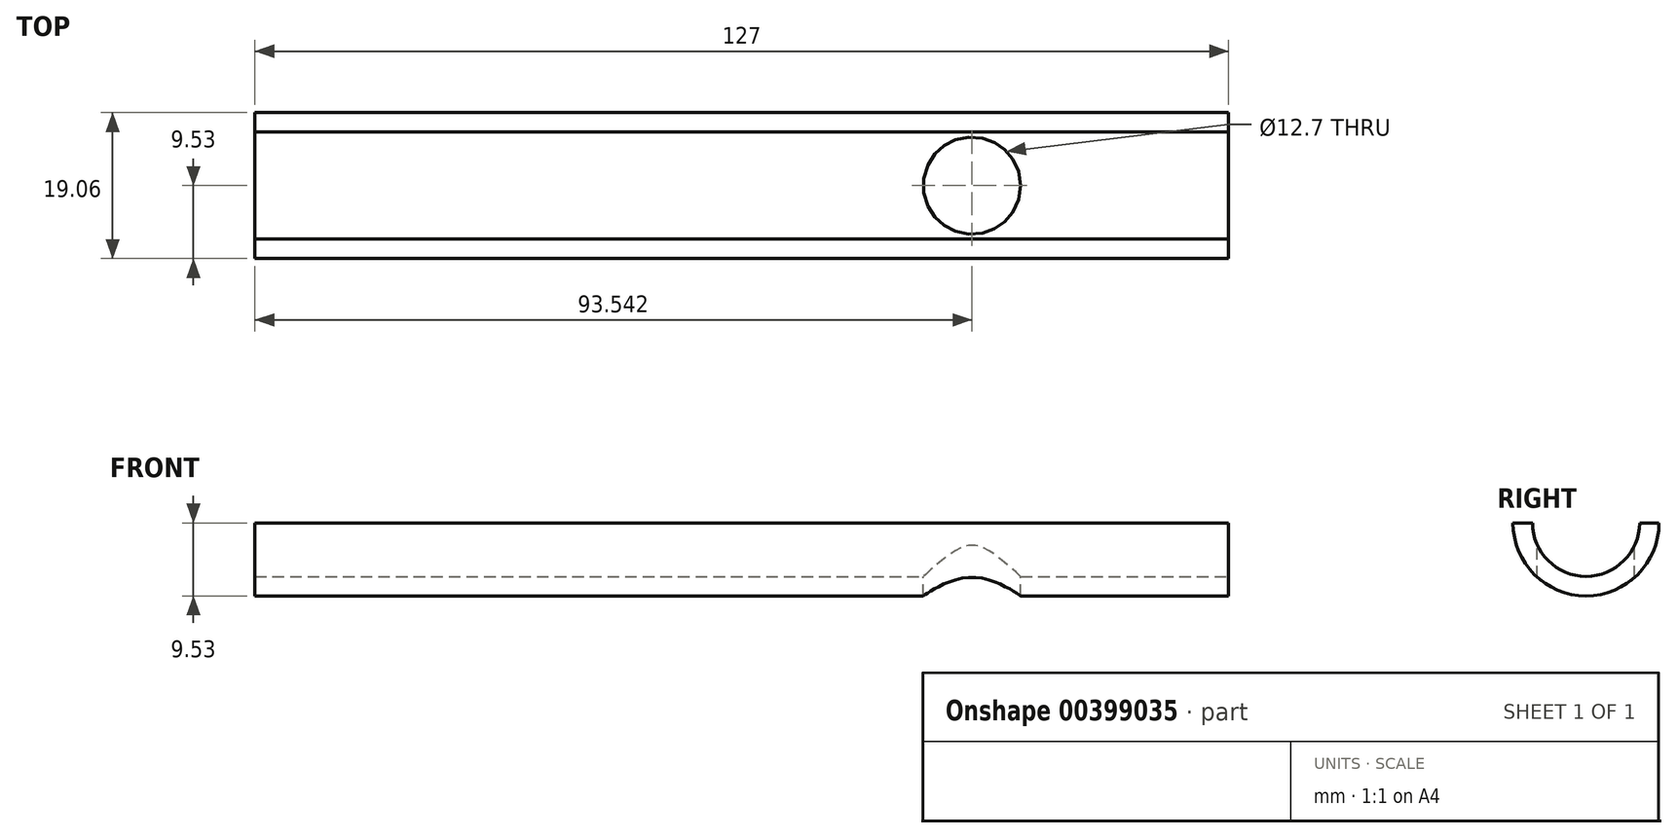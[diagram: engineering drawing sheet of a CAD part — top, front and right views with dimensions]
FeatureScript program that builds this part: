
annotation { "Feature Type Name" : "Feature", "Feature Type Description" : "" }
export const myFeature = defineFeature(function(context is Context, id is Id, definition is map)
    precondition{}
    {
        {
            var Q0;
            Q0=qCreatedBy(makeId("Right.planeOp"),FACE);
            var sketch = newSketch(context, id + "F0", { "sketchPlane" : qUnion([Q0])});
            skArc(sketch, "E0", {"start": v(-9.53, 0) * mm, "mid": v(0, -9.53) * mm, "end": v(9.53, 0) * mm});
            skLineSegment(sketch, "E1", {"start": v(-9.53, 0) * mm, "end": v(9.53, 0) * mm});
            skSolve(sketch);
        }
        {
            var Q0;
            Q0 = qSketchRegion(id + "F0", true);
            extrude(context, id + "F1", {"entities" : qUnion([Q0]), "oppositeDirection" : true, "depth" : 127 * mm, "symmetric" : true});
        }
        {
            var Q0;
            Q0=makeQuery(id+"F1.opExtrude","CAP_FACE",FACE,{"disambiguationData":[OSD([sQuery(id+"F0.wireOp",EDGE,"E0"),sQuery(id+"F0.wireOp",EDGE,"E1")])],"isStart":false});
            var Q1;
            Q1=makeQuery(id+"F1.opExtrude","SWEPT_FACE",FACE,{"disambiguationData":[OSD([sQuery(id+"F0.wireOp",EDGE,"E1")])]});
            var Q2;
            Q2=makeQuery(id+"F1.opExtrude","CAP_FACE",FACE,{"disambiguationData":[OSD([sQuery(id+"F0.wireOp",EDGE,"E0"),sQuery(id+"F0.wireOp",EDGE,"E1")])],"isStart":true});
            shell(context, id + "F2", {"entities" : qUnion([Q0, Q1, Q2]), "thickness" : 2.54 * mm});
        }
        {
            var Q0;
            Q0=qCreatedBy(makeId("Top.planeOp"),FACE);
            var sketch = newSketch(context, id + "F3", { "sketchPlane" : qUnion([Q0])});
            skCircle(sketch, "E2", {"center": v(30.04, 0) * mm, "radius": 6.35 * mm});
            skSolve(sketch);
        }
        {
            var Q0;
            Q0=makeQuery(id+"F3.imprint","IMPRINT",FACE,{"disambiguationData":[TD([[makeQuery(id+"F3.imprint","IMPRINT",EDGE,{"derivedFrom":sQuery(id+"F3.wireOp",EDGE,"E2")}),1.0]])]});
            extrude(context, id + "F4", {"entities" : qUnion([Q0]), "operationType" : NewBodyOperationType.REMOVE, "oppositeDirection" : true, "depth" : 25.4 * mm});
        }
    });
